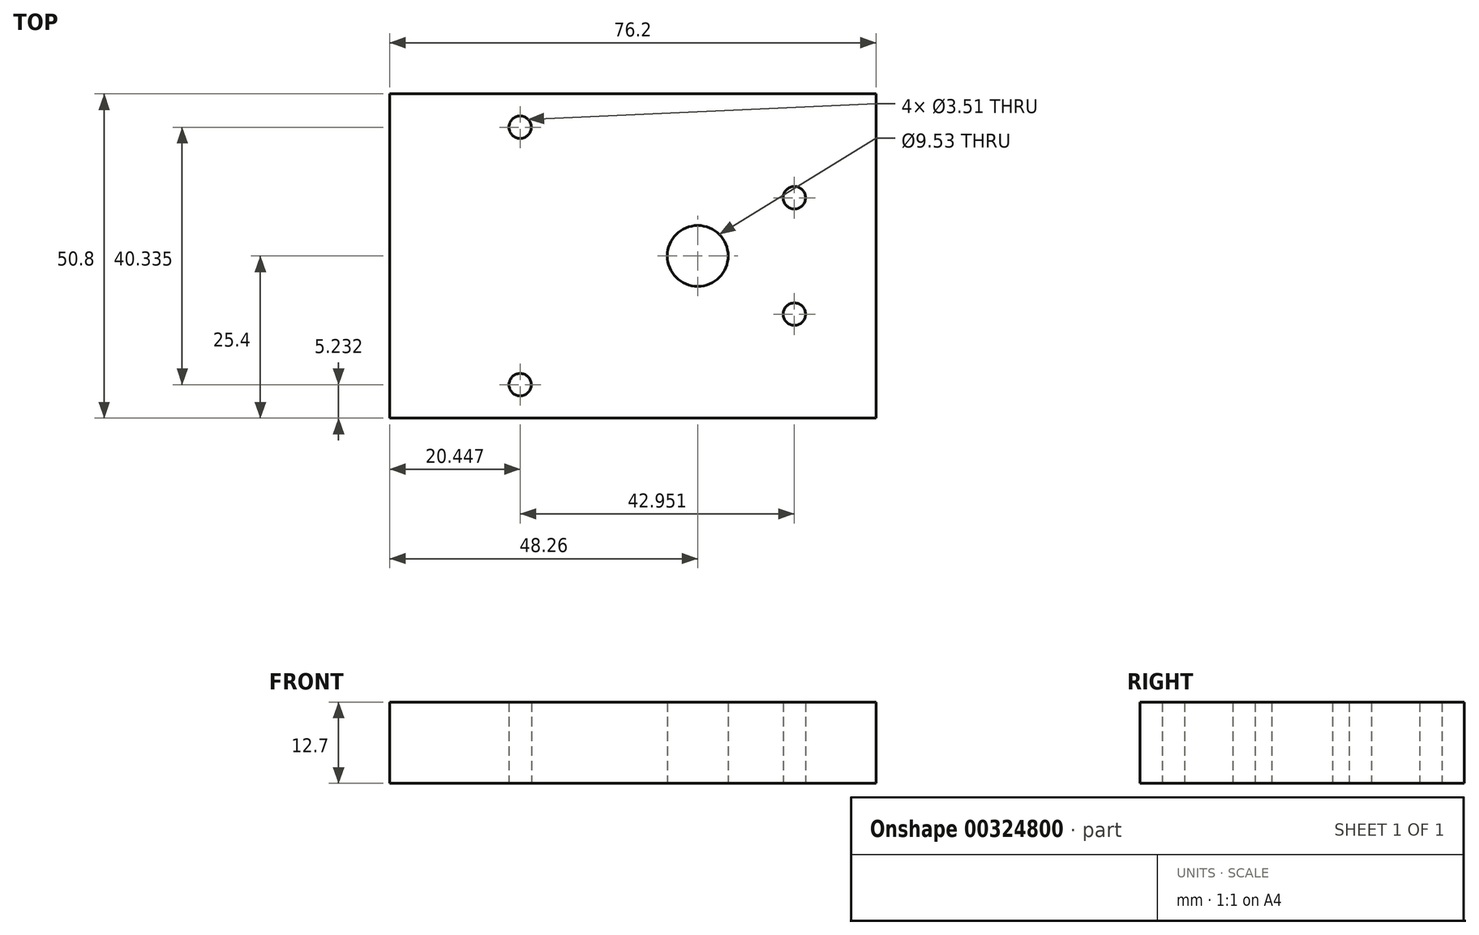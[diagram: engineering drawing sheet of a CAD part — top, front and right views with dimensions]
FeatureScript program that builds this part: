
annotation { "Feature Type Name" : "Feature", "Feature Type Description" : "" }
export const myFeature = defineFeature(function(context is Context, id is Id, definition is map)
    precondition{}
    {
        {
            var Q0;
            Q0=qCreatedBy(makeId("Top.planeOp"),FACE);
            var sketch = newSketch(context, id + "F0", { "sketchPlane" : qUnion([Q0])});
            skLineSegment(sketch, "E0", {"start": v(27.94, 25.4) * mm, "end": v(27.94, -25.4) * mm});
            skLineSegment(sketch, "E1", {"start": v(27.94, 25.4) * mm, "end": v(-48.26, 25.4) * mm});
            skLineSegment(sketch, "E2.MirrorCS", {"start": v(27.94, -25.4) * mm, "end": v(-48.26, -25.4) * mm});
            skLineSegment(sketch, "E3", {"start": v(-48.26, 25.4) * mm, "end": v(-48.26, -25.4) * mm});
            skSolve(sketch);
        }
        {
            var Q0;
            Q0=makeQuery(id+"F0.imprint","IMPRINT",FACE,{"disambiguationData":[TD([[makeQuery(id+"F0.imprint","IMPRINT",EDGE,{"derivedFrom":sQuery(id+"F0.wireOp",EDGE,"E0")}),-1.0]])]});
            extrude(context, id + "F1", {"entities" : qUnion([Q0]), "depth" : 12.7 * mm, "offsetDistance" : 25.4 * mm});
        }
        {
            var Q0;
            Q0=makeQuery(id+"F1.opExtrude","CAP_FACE",FACE,{"disambiguationData":[OSD([sQuery(id+"F0.wireOp",EDGE,"E0"),sQuery(id+"F0.wireOp",EDGE,"E1"),sQuery(id+"F0.wireOp",EDGE,"E2.MirrorCS"),sQuery(id+"F0.wireOp",EDGE,"E3")])],"isStart":false});
            var sketch = newSketch(context, id + "F2", { "sketchPlane" : qUnion([Q0])});
            skPoint(sketch, "E4", {"position": v(0, 0) * mm});
            skCircle(sketch, "E5", {"center": v(0, 0) * mm, "radius": 25.4 * mm, "construction": true});
            skLineSegment(sketch, "E6", {"start": v(-31.75, 36.12) * mm, "end": v(-31.75, -37.64) * mm, "construction": true});
            skLineSegment(sketch, "E7", {"start": v(-0.1, 25.7) * mm, "end": v(-31.75, 25.7) * mm, "construction": true});
            skLineSegment(sketch, "E8.MirrorCS", {"start": v(-0.1, -25.7) * mm, "end": v(-31.75, -25.7) * mm, "construction": true});
            skSolve(sketch);
        }
        {
            var Q0;
            Q0=sQuery(id+"F2.wireOp",VERTEX,"E4");
            var Q1;
            Q1=makeQuery(id+"F1.opExtrude","SWEPT_BODY",BODY,{"disambiguationData":[OSD([sQuery(id+"F0.wireOp",EDGE,"E0"),sQuery(id+"F0.wireOp",EDGE,"E1"),sQuery(id+"F0.wireOp",EDGE,"E2.MirrorCS"),sQuery(id+"F0.wireOp",EDGE,"E3")])]});
            hole(context, id + "F3", {"style" : HoleStyle.SIMPLE, "endStyle" : HoleEndStyle.THROUGH, "holeDiameter" : 9.52 * mm, "majorDiameter" : 6.35 * mm, "tappedDepth" : 12.7 * mm, "tapClearance" : 3, "locations" : qUnion([Q0]), "scope" : qUnion([Q1])});
        }
        {
            var Q0;
            Q0=makeQuery(id+"F1.opExtrude","CAP_FACE",FACE,{"disambiguationData":[OSD([sQuery(id+"F0.wireOp",EDGE,"E0"),sQuery(id+"F0.wireOp",EDGE,"E1"),sQuery(id+"F0.wireOp",EDGE,"E2.MirrorCS"),sQuery(id+"F0.wireOp",EDGE,"E3")])],"isStart":false});
            var sketch = newSketch(context, id + "F4", { "sketchPlane" : qUnion([Q0])});
            skPoint(sketch, "E9", {"position": v(15.14, 9.12) * mm});
            skPoint(sketch, "E10", {"position": v(15.14, -9.12) * mm});
            skPoint(sketch, "E11", {"position": v(-27.81, 20.17) * mm});
            skPoint(sketch, "E12", {"position": v(-27.81, -20.17) * mm});
            skSolve(sketch);
        }
        {
            var Q0;
            Q0=sQuery(id+"F4.wireOp",VERTEX,"E9");
            var Q1;
            Q1=sQuery(id+"F4.wireOp",VERTEX,"E10");
            var Q2;
            Q2=sQuery(id+"F4.wireOp",VERTEX,"E11");
            var Q3;
            Q3=sQuery(id+"F4.wireOp",VERTEX,"E12");
            var Q4;
            Q4=makeQuery(id+"F1.opExtrude","SWEPT_BODY",BODY,{"disambiguationData":[OSD([sQuery(id+"F0.wireOp",EDGE,"E0"),sQuery(id+"F0.wireOp",EDGE,"E1"),sQuery(id+"F0.wireOp",EDGE,"E2.MirrorCS"),sQuery(id+"F0.wireOp",EDGE,"E3")])]});
            hole(context, id + "F5", {"style" : HoleStyle.SIMPLE, "endStyle" : HoleEndStyle.THROUGH, "holeDiameter" : 3.5 * mm, "majorDiameter" : 6.35 * mm, "tappedDepth" : 12.7 * mm, "tapClearance" : 3, "locations" : qUnion([Q0, Q1, Q2, Q3]), "scope" : qUnion([Q4])});
        }
    });
